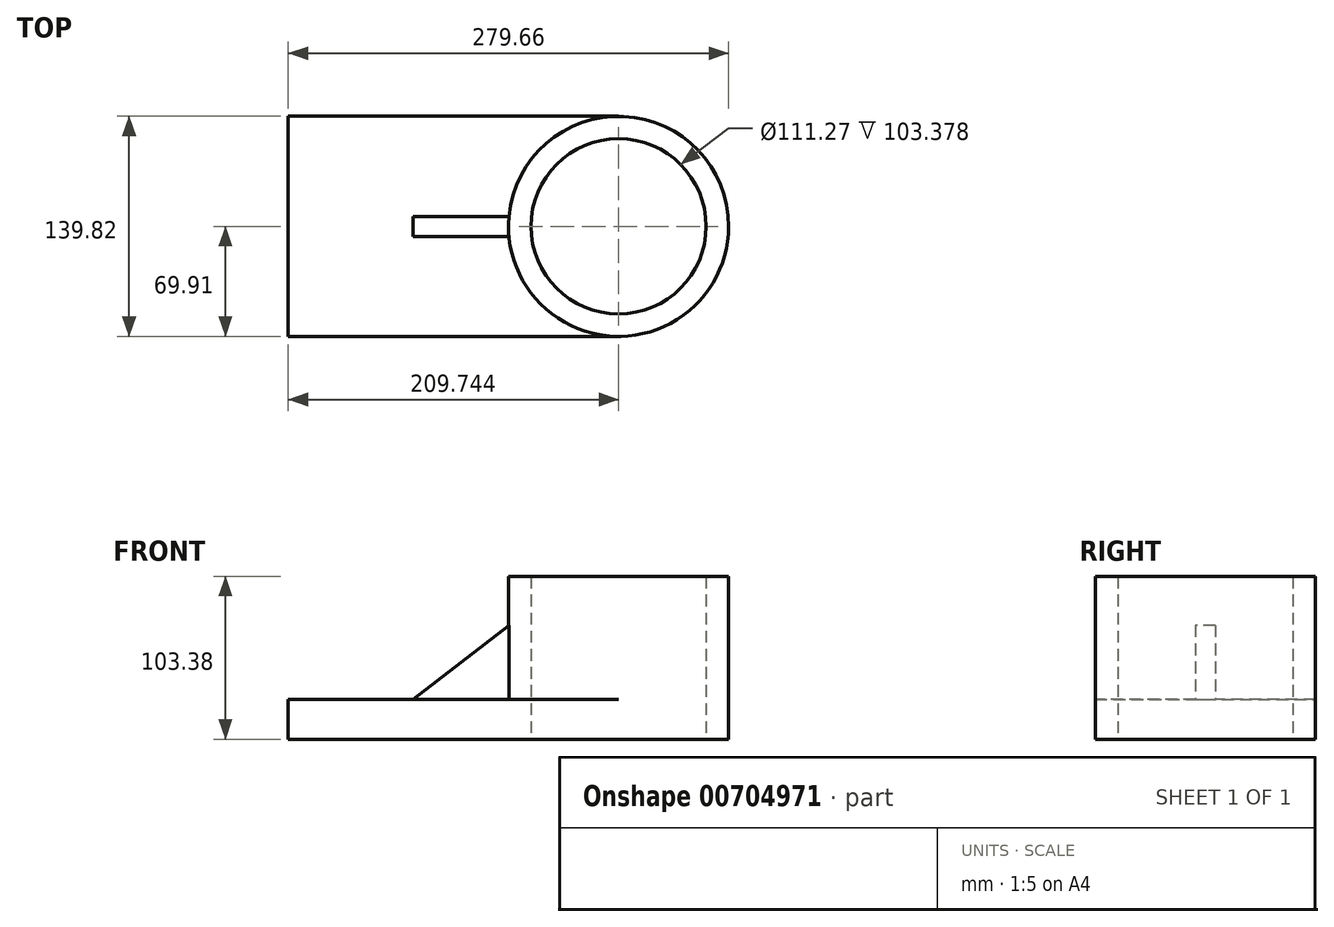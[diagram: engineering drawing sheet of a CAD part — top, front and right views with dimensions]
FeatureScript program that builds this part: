
annotation { "Feature Type Name" : "Feature", "Feature Type Description" : "" }
export const myFeature = defineFeature(function(context is Context, id is Id, definition is map)
    precondition{}
    {
        {
            var Q0;
            Q0=qCreatedBy(makeId("Top.planeOp"),FACE);
            var sketch = newSketch(context, id + "F0", { "sketchPlane" : qUnion([Q0])});
            skLineSegment(sketch, "E0.bottom", {"start": v(-139.83, -69.91) * mm, "end": v(69.91, -69.91) * mm});
            skLineSegment(sketch, "E0.top", {"start": v(-139.83, 69.91) * mm, "end": v(69.91, 69.91) * mm});
            skLineSegment(sketch, "E0.left", {"start": v(-139.83, -69.91) * mm, "end": v(-139.83, 69.91) * mm});
            skPoint(sketch, "E0.middle", {"position": v(0, 0) * mm});
            skCircle(sketch, "E1", {"center": v(69.91, 0) * mm, "radius": 69.91 * mm});
            skPoint(sketch, "E1.first.point", {"position": v(139.83, 0) * mm});
            skPoint(sketch, "E1.second.point", {"position": v(69.91, 69.91) * mm});
            skPoint(sketch, "E1.third.point", {"position": v(69.91, -69.91) * mm});
            skPoint(sketch, "E2.orphan", {"position": v(139.83, 69.91) * mm});
            skPoint(sketch, "E3.orphan", {"position": v(139.83, -69.91) * mm});
            skCircle(sketch, "E4", {"center": v(69.91, 0) * mm, "radius": 55.63 * mm});
            skSolve(sketch);
        }
        {
            var Q0;
            Q0 = qSketchRegion(id + "F0", true);
            extrude(context, id + "F1", {"entities" : qUnion([Q0]), "depth" : 25.4 * mm, "offsetDistance" : 25.4 * mm});
        }
        {
            var Q0;
            Q0=makeQuery(id+"F0.imprint","IMPRINT",FACE,{"disambiguationData":[TD([[makeQuery(id+"F0.imprint","IMPRINT",EDGE,{"derivedFrom":sQuery(id+"F0.wireOp",EDGE,"E4")}),-1.0]])]});
            extrude(context, id + "F2", {"entities" : qUnion([Q0]), "operationType" : NewBodyOperationType.ADD, "depth" : 103.38 * mm, "offsetDistance" : 25.4 * mm});
        }
        {
            var Q0;
            Q0=qCreatedBy(makeId("Front.planeOp"),FACE);
            var sketch = newSketch(context, id + "F3", { "sketchPlane" : qUnion([Q0])});
            skLineSegment(sketch, "E5.0", {"start": v(-60.48, 25.4) * mm, "end": v(14.28, 25.4) * mm});
            skLineSegment(sketch, "E6", {"start": v(14.28, 25.4) * mm, "end": v(14.28, 83.2) * mm});
            skLineSegment(sketch, "E7", {"start": v(-60.48, 25.4) * mm, "end": v(14.28, 83.2) * mm});
            skPoint(sketch, "E8.orphan", {"position": v(-139.83, 25.4) * mm});
            skSolve(sketch);
        }
        {
            var Q0;
            Q0 = qSketchRegion(id + "F3", true);
            extrude(context, id + "F4", {"entities" : qUnion([Q0]), "operationType" : NewBodyOperationType.ADD, "depth" : 6.35 * mm, "offsetDistance" : 25.4 * mm, "hasSecondDirection" : true, "secondDirectionOppositeDirection" : true, "secondDirectionDepth" : 6.35 * mm});
        }
    });
